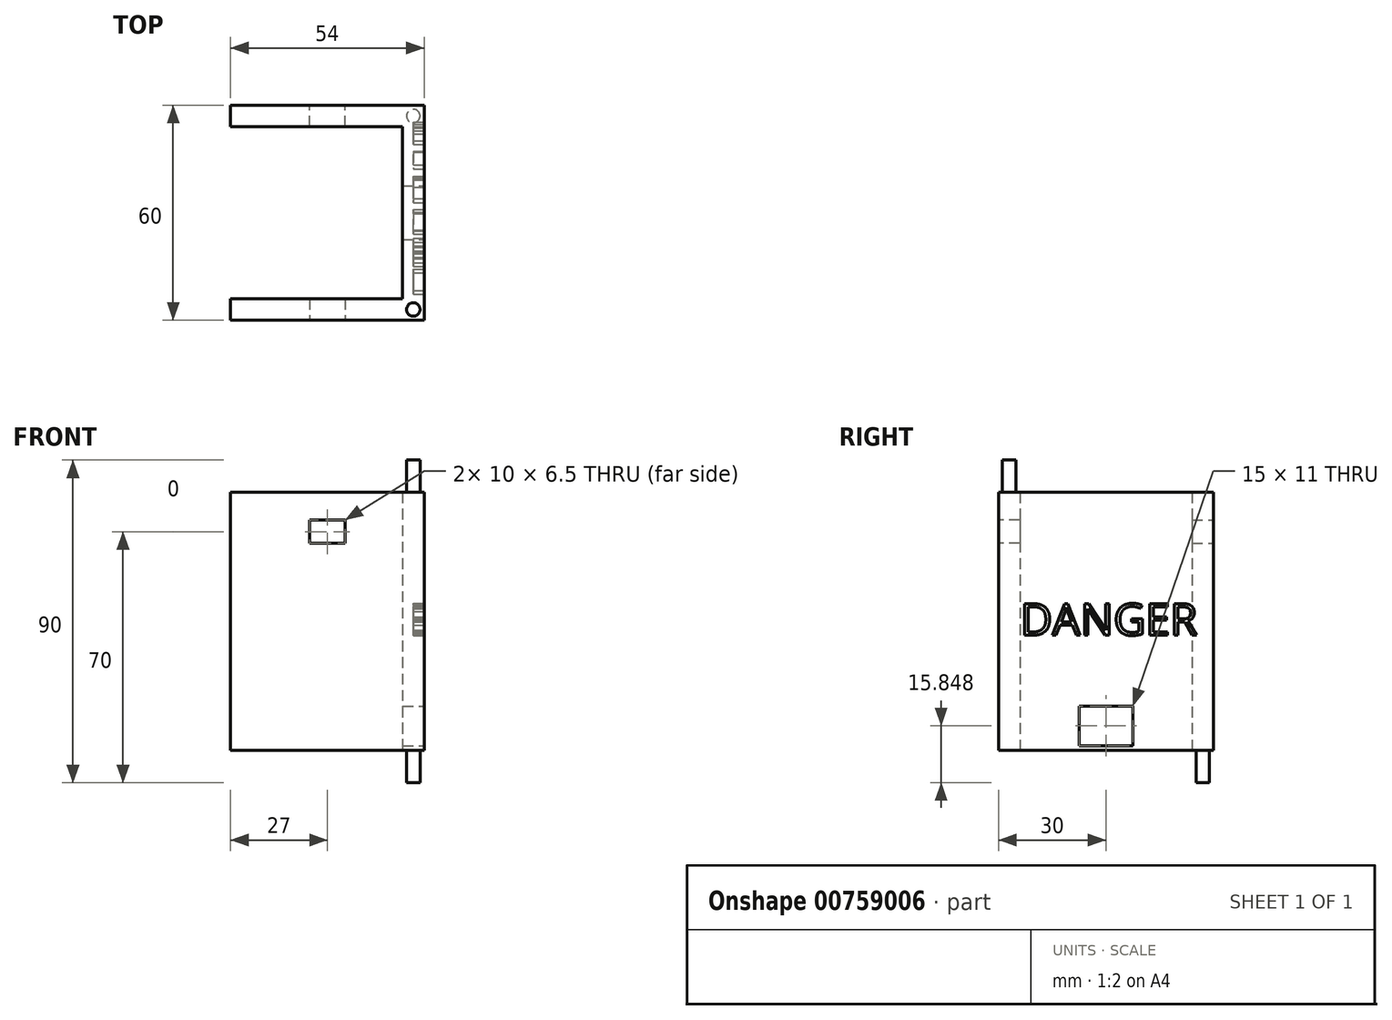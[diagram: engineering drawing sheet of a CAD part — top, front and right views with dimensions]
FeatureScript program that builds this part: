
annotation { "Feature Type Name" : "Feature", "Feature Type Description" : "" }
export const myFeature = defineFeature(function(context is Context, id is Id, definition is map)
    precondition{}
    {
        {
            var Q0;
            Q0=qCreatedBy(makeId("Top.planeOp"),FACE);
            var sketch = newSketch(context, id + "F0", { "sketchPlane" : qUnion([Q0])});
            skLineSegment(sketch, "E0.bottom", {"start": v(-27, 30) * mm, "end": v(27, 30) * mm});
            skLineSegment(sketch, "E0.top", {"start": v(-27, -30) * mm, "end": v(27, -30) * mm});
            skLineSegment(sketch, "E0.left", {"start": v(-27, 30) * mm, "end": v(-27, -30) * mm});
            skLineSegment(sketch, "E0.right", {"start": v(27, 30) * mm, "end": v(27, -30) * mm});
            skPoint(sketch, "E0.middle", {"position": v(0, 0) * mm});
            skLineSegment(sketch, "E1", {"start": v(-27, 30) * mm, "end": v(-27, 24) * mm});
            skLineSegment(sketch, "E2", {"start": v(27, 30) * mm, "end": v(27, 24) * mm});
            skLineSegment(sketch, "E3", {"start": v(-27, 24) * mm, "end": v(21, 24) * mm});
            skLineSegment(sketch, "E4", {"start": v(21, -24) * mm, "end": v(-27, -24) * mm});
            skLineSegment(sketch, "E5", {"start": v(21, 24) * mm, "end": v(21, -24) * mm});
            skSolve(sketch);
        }
        {
            var Q0;
            Q0=makeQuery(id+"F0.imprint","IMPRINT",FACE,{"disambiguationData":[TD([[makeQuery(id+"F0.imprint","IMPRINT",EDGE,{"derivedFrom":sQuery(id+"F0.wireOp",EDGE,"E0.bottom")}),-1.0]])]});
            extrude(context, id + "F1", {"entities" : qUnion([Q0]), "depth" : 90 * mm, "offsetDistance" : 25 * mm});
        }
        {
            var Q0;
            Q0=makeQuery(id+"F1.opExtrude","CAP_FACE",FACE,{"disambiguationData":[OSD([sQuery(id+"F0.wireOp",EDGE,"E0.bottom"),sQuery(id+"F0.wireOp",EDGE,"E0.top"),sQuery(id+"F0.wireOp",EDGE,"E0.left"),sQuery(id+"F0.wireOp",EDGE,"E0.right"),sQuery(id+"F0.wireOp",EDGE,"E1"),sQuery(id+"F0.wireOp",EDGE,"E2"),sQuery(id+"F0.wireOp",EDGE,"E3"),sQuery(id+"F0.wireOp",EDGE,"E4"),sQuery(id+"F0.wireOp",EDGE,"E5")])],"isStart":false});
            var sketch = newSketch(context, id + "F2", { "sketchPlane" : qUnion([Q0])});
            skCircle(sketch, "E6", {"center": v(24, 27) * mm, "radius": 1.88 * mm});
            skCircle(sketch, "E7.MirrorC", {"center": v(24, -27) * mm, "radius": 1.88 * mm});
            skSolve(sketch);
        }
        {
            var Q0;
            Q0=makeQuery(id+"F2.imprint","IMPRINT",FACE,{"disambiguationData":[TD([[makeQuery(id+"F2.imprint","IMPRINT",EDGE,{"derivedFrom":sQuery(id+"F2.wireOp",EDGE,"E6")}),1.0]])]});
            var Q1;
            Q1=makeQuery(id+"F2.imprint","IMPRINT",FACE,{"disambiguationData":[TD([[makeQuery(id+"F2.imprint","IMPRINT",EDGE,{"derivedFrom":sQuery(id+"F2.wireOp",EDGE,"E7.MirrorC")}),-1.0]])]});
            extrude(context, id + "F3", {"entities" : qUnion([Q0, Q1]), "operationType" : NewBodyOperationType.REMOVE, "oppositeDirection" : true, "depth" : 9 * mm, "offsetDistance" : 25 * mm});
        }
        {
            var Q0;
            Q0=makeQuery(id+"F1.opExtrude","CAP_FACE",FACE,{"disambiguationData":[OSD([sQuery(id+"F0.wireOp",EDGE,"E0.bottom"),sQuery(id+"F0.wireOp",EDGE,"E0.top"),sQuery(id+"F0.wireOp",EDGE,"E0.left"),sQuery(id+"F0.wireOp",EDGE,"E0.right"),sQuery(id+"F0.wireOp",EDGE,"E1"),sQuery(id+"F0.wireOp",EDGE,"E2"),sQuery(id+"F0.wireOp",EDGE,"E3"),sQuery(id+"F0.wireOp",EDGE,"E4"),sQuery(id+"F0.wireOp",EDGE,"E5")])],"isStart":true});
            var sketch = newSketch(context, id + "F4", { "sketchPlane" : qUnion([Q0])});
            skCircle(sketch, "E8", {"center": v(24, 27) * mm, "radius": 1.88 * mm});
            skCircle(sketch, "E9.MirrorC", {"center": v(24, -27) * mm, "radius": 1.88 * mm});
            skSolve(sketch);
        }
        {
            var Q0;
            Q0=makeQuery(id+"F4.imprint","IMPRINT",FACE,{"disambiguationData":[TD([[makeQuery(id+"F4.imprint","IMPRINT",EDGE,{"derivedFrom":sQuery(id+"F4.wireOp",EDGE,"E9.MirrorC")}),-1.0]])]});
            var Q1;
            Q1=makeQuery(id+"F4.imprint","IMPRINT",FACE,{"disambiguationData":[TD([[makeQuery(id+"F4.imprint","IMPRINT",EDGE,{"derivedFrom":sQuery(id+"F4.wireOp",EDGE,"E8")}),1.0]])]});
            extrude(context, id + "F5", {"entities" : qUnion([Q0, Q1]), "operationType" : NewBodyOperationType.REMOVE, "oppositeDirection" : true, "depth" : 9 * mm, "offsetDistance" : 25 * mm});
        }
        {
            var Q0;
            Q0=makeQuery(id+"F1.opExtrude","SWEPT_FACE",FACE,{"disambiguationData":[OSD([sQuery(id+"F0.wireOp",EDGE,"E0.top")])]});
            var sketch = newSketch(context, id + "F6", { "sketchPlane" : qUnion([Q0])});
            skLineSegment(sketch, "E10.bottom", {"start": v(-5, 73.25) * mm, "end": v(5, 73.25) * mm});
            skLineSegment(sketch, "E10.top", {"start": v(-5, 66.75) * mm, "end": v(5, 66.75) * mm});
            skLineSegment(sketch, "E10.left", {"start": v(-5, 73.25) * mm, "end": v(-5, 66.75) * mm});
            skLineSegment(sketch, "E10.right", {"start": v(5, 73.25) * mm, "end": v(5, 66.75) * mm});
            skPoint(sketch, "E10.middle", {"position": v(0, 70) * mm});
            skSolve(sketch);
        }
        {
            var Q0;
            Q0=makeQuery(id+"F6.imprint","IMPRINT",FACE,{"disambiguationData":[TD([[makeQuery(id+"F6.imprint","IMPRINT",EDGE,{"derivedFrom":sQuery(id+"F6.wireOp",EDGE,"E10.bottom")}),-1.0]])]});
            extrude(context, id + "F7", {"entities" : qUnion([Q0]), "operationType" : NewBodyOperationType.REMOVE, "oppositeDirection" : true, "depth" : 6 * mm, "offsetDistance" : 25 * mm});
        }
        {
            var Q0;
            Q0=makeQuery(id+"F1.opExtrude","SWEPT_FACE",FACE,{"disambiguationData":[OSD([sQuery(id+"F0.wireOp",EDGE,"E0.bottom")])]});
            var sketch = newSketch(context, id + "F8", { "sketchPlane" : qUnion([Q0])});
            skLineSegment(sketch, "E11.bottom", {"start": v(-5, 73.25) * mm, "end": v(5, 73.25) * mm});
            skLineSegment(sketch, "E11.top", {"start": v(-5, 66.75) * mm, "end": v(5, 66.75) * mm});
            skLineSegment(sketch, "E11.left", {"start": v(-5, 73.25) * mm, "end": v(-5, 66.75) * mm});
            skLineSegment(sketch, "E11.right", {"start": v(5, 73.25) * mm, "end": v(5, 66.75) * mm});
            skPoint(sketch, "E11.middle", {"position": v(0, 70) * mm});
            skSolve(sketch);
        }
        {
            var Q0;
            Q0=makeQuery(id+"F8.imprint","IMPRINT",FACE,{"disambiguationData":[TD([[makeQuery(id+"F8.imprint","IMPRINT",EDGE,{"derivedFrom":sQuery(id+"F8.wireOp",EDGE,"E11.bottom")}),-1.0]])]});
            extrude(context, id + "F9", {"entities" : qUnion([Q0]), "operationType" : NewBodyOperationType.REMOVE, "oppositeDirection" : true, "depth" : 6 * mm, "offsetDistance" : 25 * mm});
        }
        {
            var Q0;
            Q0=makeQuery(id+"F1.opExtrude","SWEPT_FACE",FACE,{"disambiguationData":[OSD([sQuery(id+"F0.wireOp",EDGE,"E0.right"),sQuery(id+"F0.wireOp",EDGE,"E2")])]});
            var sketch = newSketch(context, id + "F10", { "sketchPlane" : qUnion([Q0])});
            skText(sketch, "E12", { "text": "DANGER", "fontName": "OpenSans-Regular.ttf"});
            const initialGuessF10  = {"E12": [-0.0239, 0.04115, 1, 0, 0.00885]};
            skSetInitialGuess(sketch, initialGuessF10);
            skSolve(sketch);
        }
        {
            var Q0;
            Q0 = qSketchRegion(id + "F10", true);
            extrude(context, id + "F11", {"entities" : qUnion([Q0]), "operationType" : NewBodyOperationType.REMOVE, "oppositeDirection" : true, "depth" : 3 * mm, "offsetDistance" : 25 * mm});
        }
        {
            var Q0;
            Q0=makeQuery(id+"F10.imprint","IMPRINT",FACE,{"disambiguationData":[TD([[makeQuery(id+"F10.imprint","IMPRINT",EDGE,{"derivedFrom":sQuery(id+"F10.wireOp",EDGE,"E12.sketch_text.stroke-0")}),1.0]])]});
            var sketch = newSketch(context, id + "F12", { "sketchPlane" : qUnion([Q0])});
            skLineSegment(sketch, "E13.bottom", {"start": v(-7.5, 21.35) * mm, "end": v(7.5, 21.35) * mm});
            skLineSegment(sketch, "E13.top", {"start": v(-7.5, 10.35) * mm, "end": v(7.5, 10.35) * mm});
            skLineSegment(sketch, "E13.left", {"start": v(-7.5, 21.35) * mm, "end": v(-7.5, 10.35) * mm});
            skLineSegment(sketch, "E13.right", {"start": v(7.5, 21.35) * mm, "end": v(7.5, 10.35) * mm});
            skPoint(sketch, "E13.middle", {"position": v(0, 15.85) * mm});
            skSolve(sketch);
        }
        {
            var Q0;
            Q0=makeQuery(id+"F12.imprint","IMPRINT",FACE,{"disambiguationData":[TD([[makeQuery(id+"F12.imprint","IMPRINT",EDGE,{"derivedFrom":sQuery(id+"F12.wireOp",EDGE,"E13.bottom")}),-1.0]])]});
            extrude(context, id + "F13", {"entities" : qUnion([Q0]), "operationType" : NewBodyOperationType.REMOVE, "oppositeDirection" : true, "depth" : 6 * mm, "offsetDistance" : 25 * mm});
        }
    });
